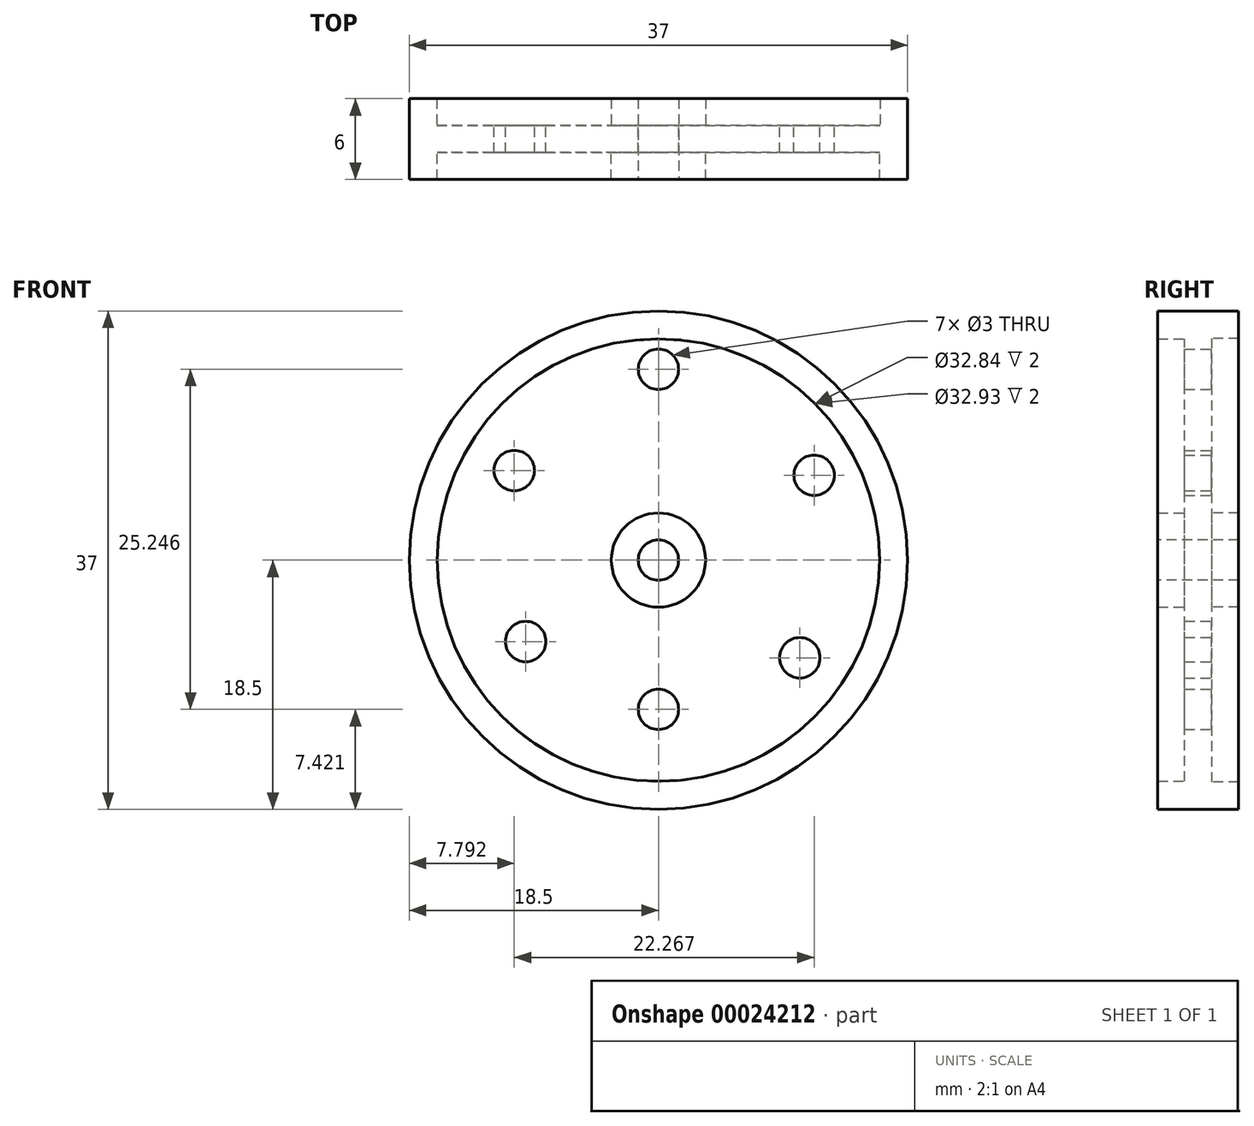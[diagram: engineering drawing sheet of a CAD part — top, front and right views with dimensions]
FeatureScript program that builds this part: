
annotation { "Feature Type Name" : "Feature", "Feature Type Description" : "" }
export const myFeature = defineFeature(function(context is Context, id is Id, definition is map)
    precondition{}
    {
        {
            var Q0;
            Q0=qCreatedBy(makeId("Front.planeOp"),FACE);
            var sketch = newSketch(context, id + "F0", { "sketchPlane" : qUnion([Q0])});
            skCircle(sketch, "E0", {"center": v(0, 0) * mm, "radius": 18.5 * mm});
            skCircle(sketch, "E1", {"center": v(0, -11.08) * mm, "radius": 1.5 * mm});
            skCircle(sketch, "E2", {"center": v(10.5, -7.25) * mm, "radius": 1.5 * mm});
            skCircle(sketch, "E3", {"center": v(0, 14.17) * mm, "radius": 1.5 * mm});
            skCircle(sketch, "E4", {"center": v(11.56, 6.3) * mm, "radius": 1.5 * mm});
            skCircle(sketch, "E5", {"center": v(-10.7, 6.65) * mm, "radius": 1.5 * mm});
            skCircle(sketch, "E6", {"center": v(-9.86, -6.04) * mm, "radius": 1.5 * mm});
            skSolve(sketch);
        }
        {
            var Q0;
            Q0 = qSketchRegion(id + "F0", true);
            extrude(context, id + "F1", {"entities" : qUnion([Q0]), "depth" : 2 * mm});
        }
        {
            var Q0;
            Q0=makeQuery(id+"F1.opExtrude","CAP_FACE",FACE,{"disambiguationData":[OSD([sQuery(id+"F0.wireOp",EDGE,"E0"),sQuery(id+"F0.wireOp",EDGE,"E1"),sQuery(id+"F0.wireOp",EDGE,"E2"),sQuery(id+"F0.wireOp",EDGE,"E3"),sQuery(id+"F0.wireOp",EDGE,"E4"),sQuery(id+"F0.wireOp",EDGE,"E5"),sQuery(id+"F0.wireOp",EDGE,"E6")])],"isStart":false});
            var sketch = newSketch(context, id + "F2", { "sketchPlane" : qUnion([Q0])});
            skCircle(sketch, "E7", {"center": v(0, 0) * mm, "radius": 3.5 * mm});
            skSolve(sketch);
        }
        {
            var Q0;
            Q0 = qSketchRegion(id + "F2", true);
            extrude(context, id + "F3", {"entities" : qUnion([Q0]), "operationType" : NewBodyOperationType.ADD, "depth" : 2 * mm});
        }
        {
            var Q0;
            Q0=makeQuery(id+"F3.opExtrude","CAP_FACE",FACE,{"disambiguationData":[OSD([sQuery(id+"F2.wireOp",EDGE,"E7")])],"isStart":false});
            var sketch = newSketch(context, id + "F4", { "sketchPlane" : qUnion([Q0])});
            skCircle(sketch, "E8", {"center": v(0, 0) * mm, "radius": 1.5 * mm});
            skSolve(sketch);
        }
        {
            var Q0;
            Q0 = qSketchRegion(id + "F4", true);
            extrude(context, id + "F5", {"entities" : qUnion([Q0]), "operationType" : NewBodyOperationType.REMOVE, "oppositeDirection" : true, "depth" : 25.4 * mm});
        }
        {
            var Q0;
            Q0=makeQuery(id+"F1.opExtrude","CAP_FACE",FACE,{"disambiguationData":[OSD([sQuery(id+"F0.wireOp",EDGE,"E0"),sQuery(id+"F0.wireOp",EDGE,"E1"),sQuery(id+"F0.wireOp",EDGE,"E2"),sQuery(id+"F0.wireOp",EDGE,"E3"),sQuery(id+"F0.wireOp",EDGE,"E4"),sQuery(id+"F0.wireOp",EDGE,"E5"),sQuery(id+"F0.wireOp",EDGE,"E6")])],"isStart":true});
            var sketch = newSketch(context, id + "F6", { "sketchPlane" : qUnion([Q0])});
            skCircle(sketch, "E9", {"center": v(0, 0) * mm, "radius": 3.5 * mm});
            skSolve(sketch);
        }
        {
            var Q0;
            Q0 = qSketchRegion(id + "F6", true);
            extrude(context, id + "F7", {"entities" : qUnion([Q0]), "operationType" : NewBodyOperationType.ADD, "depth" : 2 * mm});
        }
        {
            var Q0;
            Q0=makeQuery(id+"F7.opExtrude","CAP_FACE",FACE,{"disambiguationData":[OSD([sQuery(id+"F6.wireOp",EDGE,"E9")])],"isStart":false});
            var sketch = newSketch(context, id + "F8", { "sketchPlane" : qUnion([Q0])});
            skCircle(sketch, "E10", {"center": v(0, 0) * mm, "radius": 1.5 * mm});
            skSolve(sketch);
        }
        {
            var Q0;
            Q0 = qSketchRegion(id + "F8", true);
            extrude(context, id + "F9", {"entities" : qUnion([Q0]), "operationType" : NewBodyOperationType.REMOVE, "oppositeDirection" : true, "depth" : 25.4 * mm});
        }
        {
            var Q0;
            Q0=makeQuery(id+"F1.opExtrude","CAP_FACE",FACE,{"disambiguationData":[OSD([sQuery(id+"F0.wireOp",EDGE,"E0"),sQuery(id+"F0.wireOp",EDGE,"E1"),sQuery(id+"F0.wireOp",EDGE,"E2"),sQuery(id+"F0.wireOp",EDGE,"E3"),sQuery(id+"F0.wireOp",EDGE,"E4"),sQuery(id+"F0.wireOp",EDGE,"E5"),sQuery(id+"F0.wireOp",EDGE,"E6")])],"isStart":false});
            var sketch = newSketch(context, id + "F10", { "sketchPlane" : qUnion([Q0])});
            skCircle(sketch, "E11", {"center": v(0, 0) * mm, "radius": 16.42 * mm});
            skSolve(sketch);
        }
        {
            var Q0;
            Q0=makeQuery(id+"F10.imprint","IMPRINT",FACE,{"disambiguationData":[TD([[makeQuery(id+"F10.imprint","IMPRINT",EDGE,{"derivedFrom":sQuery(id+"F10.wireOp",EDGE,"E11")}),-1.0]])]});
            extrude(context, id + "F11", {"entities" : qUnion([Q0]), "operationType" : NewBodyOperationType.ADD, "depth" : 2 * mm});
        }
        {
            var Q0;
            Q0=makeQuery(id+"F1.opExtrude","CAP_FACE",FACE,{"disambiguationData":[OSD([sQuery(id+"F0.wireOp",EDGE,"E0"),sQuery(id+"F0.wireOp",EDGE,"E1"),sQuery(id+"F0.wireOp",EDGE,"E2"),sQuery(id+"F0.wireOp",EDGE,"E3"),sQuery(id+"F0.wireOp",EDGE,"E4"),sQuery(id+"F0.wireOp",EDGE,"E5"),sQuery(id+"F0.wireOp",EDGE,"E6")])],"isStart":true});
            var sketch = newSketch(context, id + "F12", { "sketchPlane" : qUnion([Q0])});
            skCircle(sketch, "E12", {"center": v(0, 0) * mm, "radius": 16.46 * mm});
            skSolve(sketch);
        }
        {
            var Q0;
            Q0=makeQuery(id+"F12.imprint","IMPRINT",FACE,{"disambiguationData":[TD([[makeQuery(id+"F12.imprint","IMPRINT",EDGE,{"derivedFrom":sQuery(id+"F12.wireOp",EDGE,"E12")}),-1.0]])]});
            extrude(context, id + "F13", {"entities" : qUnion([Q0]), "operationType" : NewBodyOperationType.ADD, "depth" : 2 * mm});
        }
    });
